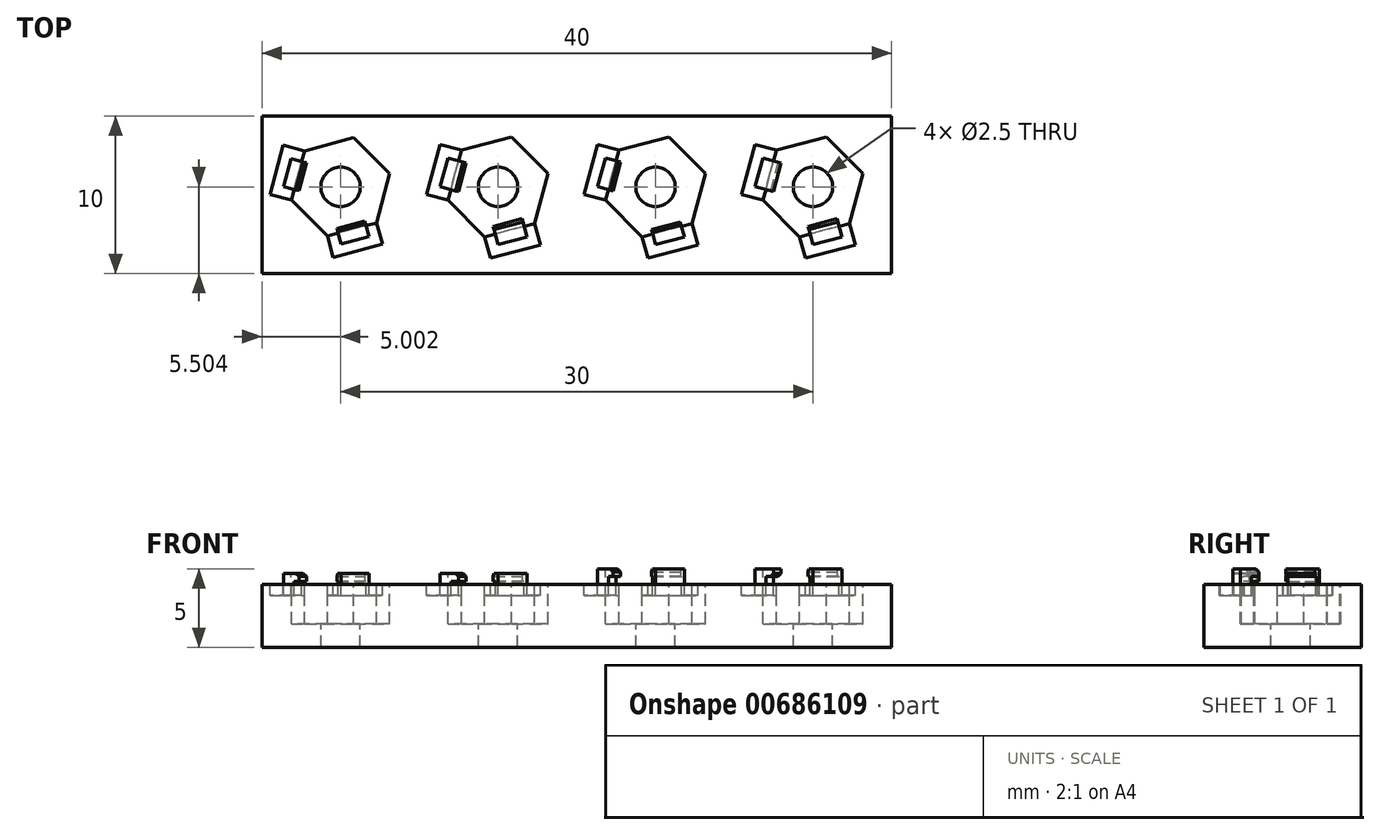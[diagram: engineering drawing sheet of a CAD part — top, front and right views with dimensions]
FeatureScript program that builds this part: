
annotation { "Feature Type Name" : "Feature", "Feature Type Description" : "" }
export const myFeature = defineFeature(function(context is Context, id is Id, definition is map)
    precondition{}
    {
        {
            var Q0;
            Q0=qCreatedBy(makeId("Top.planeOp"),FACE);
            var sketch = newSketch(context, id + "F0", { "sketchPlane" : qUnion([Q0])});
            skLineSegment(sketch, "E0.bottom", {"start": v(-19.43, 38.27) * mm, "end": v(20.57, 38.27) * mm});
            skLineSegment(sketch, "E0.top", {"start": v(-19.43, 28.27) * mm, "end": v(20.57, 28.27) * mm});
            skLineSegment(sketch, "E0.left", {"start": v(-19.43, 38.27) * mm, "end": v(-19.43, 28.27) * mm});
            skLineSegment(sketch, "E0.right", {"start": v(20.57, 38.27) * mm, "end": v(20.57, 28.27) * mm});
            skSolve(sketch);
        }
        {
            var Q0;
            Q0=makeQuery(id+"F0.imprint","IMPRINT",FACE,{"disambiguationData":[TD([[makeQuery(id+"F0.imprint","IMPRINT",EDGE,{"derivedFrom":sQuery(id+"F0.wireOp",EDGE,"E0.bottom")}),-1.0]])]});
            extrude(context, id + "F1", {"entities" : qUnion([Q0]), "depth" : 4 * mm, "offsetDistance" : 25 * mm});
        }
        {
            var Q0;
            Q0=makeQuery(id+"F1.opExtrude","CAP_FACE",FACE,{"disambiguationData":[OSD([sQuery(id+"F0.wireOp",EDGE,"E0.bottom"),sQuery(id+"F0.wireOp",EDGE,"E0.top"),sQuery(id+"F0.wireOp",EDGE,"E0.left"),sQuery(id+"F0.wireOp",EDGE,"E0.right")])],"isStart":false});
            var sketch = newSketch(context, id + "F2", { "sketchPlane" : qUnion([Q0])});
            skCircle(sketch, "E1.cCircle", {"center": v(-14.43, 33.77) * mm, "radius": 2.8 * mm, "construction": true});
            skLineSegment(sketch, "E1.0", {"start": v(-15.27, 30.65) * mm, "end": v(-17.55, 32.94) * mm});
            skLineSegment(sketch, "E1.1", {"start": v(-17.55, 32.94) * mm, "end": v(-16.71, 36.06) * mm});
            skLineSegment(sketch, "E1.2", {"start": v(-16.71, 36.06) * mm, "end": v(-13.6, 36.9) * mm});
            skLineSegment(sketch, "E1.3", {"start": v(-13.6, 36.9) * mm, "end": v(-11.3, 34.61) * mm});
            skLineSegment(sketch, "E1.4", {"start": v(-11.3, 34.61) * mm, "end": v(-12.14, 31.49) * mm});
            skLineSegment(sketch, "E1.5", {"start": v(-12.14, 31.49) * mm, "end": v(-15.27, 30.65) * mm});
            skPoint(sketch, "E1.0.midPoint", {"position": v(-16.4, 31.8) * mm});
            skLineSegment(sketch, "E2", {"start": v(-16.9, 35.38) * mm, "end": v(-17.57, 35.57) * mm});
            skLineSegment(sketch, "E3", {"start": v(-17.57, 35.57) * mm, "end": v(-18.05, 33.8) * mm});
            skLineSegment(sketch, "E4", {"start": v(-18.05, 33.8) * mm, "end": v(-17.37, 33.61) * mm});
            skLineSegment(sketch, "E5", {"start": v(-17.55, 32.94) * mm, "end": v(-18.9, 33.3) * mm});
            skLineSegment(sketch, "E6", {"start": v(-18.9, 33.3) * mm, "end": v(-18.07, 36.42) * mm});
            skLineSegment(sketch, "E7", {"start": v(-18.07, 36.42) * mm, "end": v(-16.71, 36.06) * mm});
            skLineSegment(sketch, "E8", {"start": v(-17.37, 33.61) * mm, "end": v(-17.08, 33.54) * mm});
            skLineSegment(sketch, "E9", {"start": v(-17.08, 33.54) * mm, "end": v(-16.6, 35.3) * mm});
            skLineSegment(sketch, "E10", {"start": v(-16.6, 35.3) * mm, "end": v(-16.9, 35.38) * mm});
            skLineSegment(sketch, "E11", {"start": v(-15.27, 30.65) * mm, "end": v(-14.9, 29.3) * mm});
            skLineSegment(sketch, "E12", {"start": v(-14.9, 29.3) * mm, "end": v(-11.78, 30.14) * mm});
            skLineSegment(sketch, "E13", {"start": v(-11.78, 30.14) * mm, "end": v(-12.14, 31.49) * mm});
            skLineSegment(sketch, "E14", {"start": v(-14.59, 30.83) * mm, "end": v(-14.4, 30.16) * mm});
            skLineSegment(sketch, "E15", {"start": v(-14.4, 30.16) * mm, "end": v(-12.64, 30.63) * mm});
            skLineSegment(sketch, "E16", {"start": v(-12.64, 30.63) * mm, "end": v(-12.82, 31.3) * mm});
            skLineSegment(sketch, "E17", {"start": v(-14.59, 30.83) * mm, "end": v(-14.67, 31.12) * mm});
            skLineSegment(sketch, "E18", {"start": v(-14.67, 31.12) * mm, "end": v(-12.9, 31.6) * mm});
            skLineSegment(sketch, "E19", {"start": v(-12.9, 31.6) * mm, "end": v(-12.82, 31.3) * mm});
            skCircle(sketch, "E20.cCircle", {"center": v(-4.43, 33.77) * mm, "radius": 2.85 * mm, "construction": true});
            skLineSegment(sketch, "E20.0", {"start": v(-5.28, 30.6) * mm, "end": v(-7.6, 32.92) * mm});
            skLineSegment(sketch, "E20.1", {"start": v(-7.6, 32.92) * mm, "end": v(-6.76, 36.1) * mm});
            skLineSegment(sketch, "E20.2", {"start": v(-6.76, 36.1) * mm, "end": v(-3.58, 36.95) * mm});
            skLineSegment(sketch, "E20.3", {"start": v(-3.58, 36.95) * mm, "end": v(-1.25, 34.63) * mm});
            skLineSegment(sketch, "E20.4", {"start": v(-1.25, 34.63) * mm, "end": v(-2.1, 31.45) * mm});
            skLineSegment(sketch, "E20.5", {"start": v(-2.1, 31.45) * mm, "end": v(-5.28, 30.6) * mm});
            skPoint(sketch, "E20.0.midPoint", {"position": v(-6.44, 31.76) * mm});
            skLineSegment(sketch, "E21", {"start": v(-6.94, 35.42) * mm, "end": v(-7.61, 35.6) * mm});
            skLineSegment(sketch, "E22", {"start": v(-7.61, 35.6) * mm, "end": v(-8.1, 33.78) * mm});
            skLineSegment(sketch, "E23", {"start": v(-8.1, 33.78) * mm, "end": v(-7.43, 33.6) * mm});
            skLineSegment(sketch, "E24", {"start": v(-7.6, 32.92) * mm, "end": v(-8.96, 33.28) * mm});
            skLineSegment(sketch, "E25", {"start": v(-8.96, 33.28) * mm, "end": v(-8.1, 36.46) * mm});
            skLineSegment(sketch, "E26", {"start": v(-8.1, 36.46) * mm, "end": v(-6.76, 36.1) * mm});
            skLineSegment(sketch, "E27", {"start": v(-7.43, 33.6) * mm, "end": v(-7.04, 33.5) * mm});
            skLineSegment(sketch, "E28", {"start": v(-7.04, 33.5) * mm, "end": v(-6.55, 35.32) * mm});
            skLineSegment(sketch, "E29", {"start": v(-6.55, 35.32) * mm, "end": v(-6.94, 35.42) * mm});
            skLineSegment(sketch, "E30", {"start": v(-5.28, 30.6) * mm, "end": v(-4.92, 29.24) * mm});
            skLineSegment(sketch, "E31", {"start": v(-4.92, 29.24) * mm, "end": v(-1.74, 30.1) * mm});
            skLineSegment(sketch, "E32", {"start": v(-1.74, 30.1) * mm, "end": v(-2.1, 31.45) * mm});
            skLineSegment(sketch, "E33", {"start": v(-4.6, 30.78) * mm, "end": v(-4.42, 30.1) * mm});
            skLineSegment(sketch, "E34", {"start": v(-4.42, 30.1) * mm, "end": v(-2.6, 30.59) * mm});
            skLineSegment(sketch, "E35", {"start": v(-2.6, 30.59) * mm, "end": v(-2.78, 31.27) * mm});
            skLineSegment(sketch, "E36", {"start": v(-4.6, 30.78) * mm, "end": v(-4.7, 31.16) * mm});
            skLineSegment(sketch, "E37", {"start": v(-4.7, 31.16) * mm, "end": v(-2.88, 31.65) * mm});
            skLineSegment(sketch, "E38", {"start": v(-2.88, 31.65) * mm, "end": v(-2.78, 31.27) * mm});
            skCircle(sketch, "E39.cCircle", {"center": v(5.57, 33.77) * mm, "radius": 2.85 * mm, "construction": true});
            skLineSegment(sketch, "E39.0", {"start": v(4.72, 30.6) * mm, "end": v(2.4, 32.92) * mm});
            skLineSegment(sketch, "E39.1", {"start": v(2.4, 32.92) * mm, "end": v(3.24, 36.1) * mm});
            skLineSegment(sketch, "E39.2", {"start": v(3.24, 36.1) * mm, "end": v(6.42, 36.95) * mm});
            skLineSegment(sketch, "E39.3", {"start": v(6.42, 36.95) * mm, "end": v(8.75, 34.63) * mm});
            skLineSegment(sketch, "E39.4", {"start": v(8.75, 34.63) * mm, "end": v(7.9, 31.45) * mm});
            skLineSegment(sketch, "E39.5", {"start": v(7.9, 31.45) * mm, "end": v(4.72, 30.6) * mm});
            skPoint(sketch, "E39.0.midPoint", {"position": v(3.56, 31.76) * mm});
            skLineSegment(sketch, "E40", {"start": v(3.06, 35.42) * mm, "end": v(2.39, 35.6) * mm});
            skLineSegment(sketch, "E41", {"start": v(2.39, 35.6) * mm, "end": v(1.9, 33.78) * mm});
            skLineSegment(sketch, "E42", {"start": v(1.9, 33.78) * mm, "end": v(2.57, 33.6) * mm});
            skLineSegment(sketch, "E43", {"start": v(2.4, 32.92) * mm, "end": v(1.04, 33.28) * mm});
            skLineSegment(sketch, "E44", {"start": v(1.04, 33.28) * mm, "end": v(1.9, 36.46) * mm});
            skLineSegment(sketch, "E45", {"start": v(1.9, 36.46) * mm, "end": v(3.24, 36.1) * mm});
            skLineSegment(sketch, "E46", {"start": v(2.57, 33.6) * mm, "end": v(2.96, 33.5) * mm});
            skLineSegment(sketch, "E47", {"start": v(2.96, 33.5) * mm, "end": v(3.45, 35.32) * mm});
            skLineSegment(sketch, "E48", {"start": v(3.45, 35.32) * mm, "end": v(3.06, 35.42) * mm});
            skLineSegment(sketch, "E49", {"start": v(4.72, 30.6) * mm, "end": v(5.08, 29.24) * mm});
            skLineSegment(sketch, "E50", {"start": v(5.08, 29.24) * mm, "end": v(8.26, 30.1) * mm});
            skLineSegment(sketch, "E51", {"start": v(8.26, 30.1) * mm, "end": v(7.9, 31.45) * mm});
            skLineSegment(sketch, "E52", {"start": v(5.4, 30.78) * mm, "end": v(5.58, 30.1) * mm});
            skLineSegment(sketch, "E53", {"start": v(5.58, 30.1) * mm, "end": v(7.4, 30.59) * mm});
            skLineSegment(sketch, "E54", {"start": v(7.4, 30.59) * mm, "end": v(7.22, 31.27) * mm});
            skLineSegment(sketch, "E55", {"start": v(5.4, 30.78) * mm, "end": v(5.3, 31.16) * mm});
            skLineSegment(sketch, "E56", {"start": v(5.3, 31.16) * mm, "end": v(7.12, 31.65) * mm});
            skLineSegment(sketch, "E57", {"start": v(7.12, 31.65) * mm, "end": v(7.22, 31.27) * mm});
            skCircle(sketch, "E58.cCircle", {"center": v(15.57, 33.77) * mm, "radius": 2.85 * mm, "construction": true});
            skLineSegment(sketch, "E58.0", {"start": v(14.72, 30.6) * mm, "end": v(12.4, 32.92) * mm});
            skLineSegment(sketch, "E58.1", {"start": v(12.4, 32.92) * mm, "end": v(13.24, 36.1) * mm});
            skLineSegment(sketch, "E58.2", {"start": v(13.24, 36.1) * mm, "end": v(16.42, 36.95) * mm});
            skLineSegment(sketch, "E58.3", {"start": v(16.42, 36.95) * mm, "end": v(18.75, 34.63) * mm});
            skLineSegment(sketch, "E58.4", {"start": v(18.75, 34.63) * mm, "end": v(17.9, 31.45) * mm});
            skLineSegment(sketch, "E58.5", {"start": v(17.9, 31.45) * mm, "end": v(14.72, 30.6) * mm});
            skPoint(sketch, "E58.0.midPoint", {"position": v(13.56, 31.76) * mm});
            skLineSegment(sketch, "E59", {"start": v(13.06, 35.42) * mm, "end": v(12.39, 35.6) * mm});
            skLineSegment(sketch, "E60", {"start": v(12.39, 35.6) * mm, "end": v(11.9, 33.78) * mm});
            skLineSegment(sketch, "E61", {"start": v(11.9, 33.78) * mm, "end": v(12.57, 33.6) * mm});
            skLineSegment(sketch, "E62", {"start": v(12.4, 32.92) * mm, "end": v(11.04, 33.28) * mm});
            skLineSegment(sketch, "E63", {"start": v(11.04, 33.28) * mm, "end": v(11.9, 36.46) * mm});
            skLineSegment(sketch, "E64", {"start": v(11.9, 36.46) * mm, "end": v(13.24, 36.1) * mm});
            skLineSegment(sketch, "E65", {"start": v(12.57, 33.6) * mm, "end": v(13.06, 33.47) * mm});
            skLineSegment(sketch, "E66", {"start": v(13.06, 33.47) * mm, "end": v(13.55, 35.3) * mm});
            skLineSegment(sketch, "E67", {"start": v(13.55, 35.3) * mm, "end": v(13.06, 35.42) * mm});
            skLineSegment(sketch, "E68", {"start": v(14.72, 30.6) * mm, "end": v(15.08, 29.24) * mm});
            skLineSegment(sketch, "E69", {"start": v(15.08, 29.24) * mm, "end": v(18.26, 30.1) * mm});
            skLineSegment(sketch, "E70", {"start": v(18.26, 30.1) * mm, "end": v(17.9, 31.45) * mm});
            skLineSegment(sketch, "E71", {"start": v(15.4, 30.78) * mm, "end": v(15.58, 30.1) * mm});
            skLineSegment(sketch, "E72", {"start": v(15.58, 30.1) * mm, "end": v(17.4, 30.59) * mm});
            skLineSegment(sketch, "E73", {"start": v(17.4, 30.59) * mm, "end": v(17.22, 31.27) * mm});
            skLineSegment(sketch, "E74", {"start": v(15.4, 30.78) * mm, "end": v(15.27, 31.26) * mm});
            skLineSegment(sketch, "E75", {"start": v(15.27, 31.26) * mm, "end": v(17.1, 31.75) * mm});
            skLineSegment(sketch, "E76", {"start": v(17.1, 31.75) * mm, "end": v(17.22, 31.27) * mm});
            skLineSegment(sketch, "E77", {"start": v(-14.43, 33.77) * mm, "end": v(-14.43, 38.27) * mm, "construction": true});
            skLineSegment(sketch, "E78", {"start": v(-4.43, 33.77) * mm, "end": v(-4.43, 38.27) * mm, "construction": true});
            skLineSegment(sketch, "E79", {"start": v(5.57, 33.77) * mm, "end": v(5.57, 38.27) * mm, "construction": true});
            skLineSegment(sketch, "E80", {"start": v(15.57, 33.77) * mm, "end": v(15.57, 38.27) * mm, "construction": true});
            skCircle(sketch, "E81", {"center": v(-14.43, 33.77) * mm, "radius": 1.25 * mm});
            skCircle(sketch, "E82", {"center": v(-4.43, 33.77) * mm, "radius": 1.25 * mm});
            skCircle(sketch, "E83", {"center": v(5.57, 33.77) * mm, "radius": 1.25 * mm});
            skCircle(sketch, "E84", {"center": v(15.57, 33.77) * mm, "radius": 1.25 * mm});
            skSolve(sketch);
        }
        {
            var Q0;
            {var subQ1=sQuery(id+"F2.wireOp",EDGE,"E1.0");Q0=makeQuery(id+"F2.imprint","IMPRINT",FACE,{"disambiguationData":[TD([[makeQuery(id+"F2.imprint","IMPRINT",EDGE,{"derivedFrom":subQ1}),-1.0]])]});}
            var Q1;
            {var subQ0=sQuery(id+"F2.wireOp",EDGE,"E17");Q1=makeQuery(id+"F2.imprint","IMPRINT",FACE,{"disambiguationData":[TD([[makeQuery(id+"F2.imprint","IMPRINT",EDGE,{"derivedFrom":subQ0}),-1.0]])]});}
            var Q2;
            {var subQ2=sQuery(id+"F2.wireOp",EDGE,"E8");Q2=makeQuery(id+"F2.imprint","IMPRINT",FACE,{"disambiguationData":[TD([[makeQuery(id+"F2.imprint","IMPRINT",EDGE,{"derivedFrom":subQ2}),1.0]])]});}
            var Q3;
            {var subQ1=sQuery(id+"F2.wireOp",EDGE,"E20.0");Q3=makeQuery(id+"F2.imprint","IMPRINT",FACE,{"disambiguationData":[TD([[makeQuery(id+"F2.imprint","IMPRINT",EDGE,{"derivedFrom":subQ1}),-1.0]])]});}
            var Q4;
            {var subQ0=sQuery(id+"F2.wireOp",EDGE,"E36");Q4=makeQuery(id+"F2.imprint","IMPRINT",FACE,{"disambiguationData":[TD([[makeQuery(id+"F2.imprint","IMPRINT",EDGE,{"derivedFrom":subQ0}),-1.0]])]});}
            var Q5;
            {var subQ2=sQuery(id+"F2.wireOp",EDGE,"E27");Q5=makeQuery(id+"F2.imprint","IMPRINT",FACE,{"disambiguationData":[TD([[makeQuery(id+"F2.imprint","IMPRINT",EDGE,{"derivedFrom":subQ2}),1.0]])]});}
            var Q6;
            {var subQ1=sQuery(id+"F2.wireOp",EDGE,"E39.0");Q6=makeQuery(id+"F2.imprint","IMPRINT",FACE,{"disambiguationData":[TD([[makeQuery(id+"F2.imprint","IMPRINT",EDGE,{"derivedFrom":subQ1}),-1.0]])]});}
            var Q7;
            {var subQ2=sQuery(id+"F2.wireOp",EDGE,"E46");Q7=makeQuery(id+"F2.imprint","IMPRINT",FACE,{"disambiguationData":[TD([[makeQuery(id+"F2.imprint","IMPRINT",EDGE,{"derivedFrom":subQ2}),1.0]])]});}
            var Q8;
            {var subQ0=sQuery(id+"F2.wireOp",EDGE,"E55");Q8=makeQuery(id+"F2.imprint","IMPRINT",FACE,{"disambiguationData":[TD([[makeQuery(id+"F2.imprint","IMPRINT",EDGE,{"derivedFrom":subQ0}),-1.0]])]});}
            var Q9;
            {var subQ1=sQuery(id+"F2.wireOp",EDGE,"E58.0");Q9=makeQuery(id+"F2.imprint","IMPRINT",FACE,{"disambiguationData":[TD([[makeQuery(id+"F2.imprint","IMPRINT",EDGE,{"derivedFrom":subQ1}),-1.0]])]});}
            var Q10;
            {var subQ0=sQuery(id+"F2.wireOp",EDGE,"E74");Q10=makeQuery(id+"F2.imprint","IMPRINT",FACE,{"disambiguationData":[TD([[makeQuery(id+"F2.imprint","IMPRINT",EDGE,{"derivedFrom":subQ0}),-1.0]])]});}
            var Q11;
            {var subQ2=sQuery(id+"F2.wireOp",EDGE,"E65");Q11=makeQuery(id+"F2.imprint","IMPRINT",FACE,{"disambiguationData":[TD([[makeQuery(id+"F2.imprint","IMPRINT",EDGE,{"derivedFrom":subQ2}),1.0]])]});}
            extrude(context, id + "F3", {"entities" : qUnion([Q0, Q1, Q2, Q3, Q4, Q5, Q6, Q7, Q8, Q9, Q10, Q11]), "operationType" : NewBodyOperationType.REMOVE, "oppositeDirection" : true, "depth" : 2.5 * mm, "offsetDistance" : 25 * mm});
        }
        {
            var Q0;
            {var subQ0=sQuery(id+"F2.wireOp",EDGE,"E2");Q0=makeQuery(id+"F2.imprint","IMPRINT",FACE,{"disambiguationData":[TD([[makeQuery(id+"F2.imprint","IMPRINT",EDGE,{"derivedFrom":subQ0}),-1.0]])]});}
            var Q1;
            {var subQ0=sQuery(id+"F2.wireOp",EDGE,"E11");Q1=makeQuery(id+"F2.imprint","IMPRINT",FACE,{"disambiguationData":[TD([[makeQuery(id+"F2.imprint","IMPRINT",EDGE,{"derivedFrom":subQ0}),1.0]])]});}
            var Q2;
            {var subQ0=sQuery(id+"F2.wireOp",EDGE,"E30");Q2=makeQuery(id+"F2.imprint","IMPRINT",FACE,{"disambiguationData":[TD([[makeQuery(id+"F2.imprint","IMPRINT",EDGE,{"derivedFrom":subQ0}),1.0]])]});}
            var Q3;
            {var subQ0=sQuery(id+"F2.wireOp",EDGE,"E21");Q3=makeQuery(id+"F2.imprint","IMPRINT",FACE,{"disambiguationData":[TD([[makeQuery(id+"F2.imprint","IMPRINT",EDGE,{"derivedFrom":subQ0}),-1.0]])]});}
            var Q4;
            {var subQ0=sQuery(id+"F2.wireOp",EDGE,"E40");Q4=makeQuery(id+"F2.imprint","IMPRINT",FACE,{"disambiguationData":[TD([[makeQuery(id+"F2.imprint","IMPRINT",EDGE,{"derivedFrom":subQ0}),-1.0]])]});}
            var Q5;
            {var subQ0=sQuery(id+"F2.wireOp",EDGE,"E49");Q5=makeQuery(id+"F2.imprint","IMPRINT",FACE,{"disambiguationData":[TD([[makeQuery(id+"F2.imprint","IMPRINT",EDGE,{"derivedFrom":subQ0}),1.0]])]});}
            var Q6;
            {var subQ0=sQuery(id+"F2.wireOp",EDGE,"E68");Q6=makeQuery(id+"F2.imprint","IMPRINT",FACE,{"disambiguationData":[TD([[makeQuery(id+"F2.imprint","IMPRINT",EDGE,{"derivedFrom":subQ0}),1.0]])]});}
            var Q7;
            {var subQ0=sQuery(id+"F2.wireOp",EDGE,"E59");Q7=makeQuery(id+"F2.imprint","IMPRINT",FACE,{"disambiguationData":[TD([[makeQuery(id+"F2.imprint","IMPRINT",EDGE,{"derivedFrom":subQ0}),-1.0]])]});}
            extrude(context, id + "F4", {"entities" : qUnion([Q0, Q1, Q2, Q3, Q4, Q5, Q6, Q7]), "operationType" : NewBodyOperationType.REMOVE, "oppositeDirection" : true, "depth" : .7 * mm, "offsetDistance" : 25 * mm});
        }
        {
            var Q0;
            {var subQ0=sQuery(id+"F2.wireOp",EDGE,"E2");Q0=makeQuery(id+"F2.imprint","IMPRINT",FACE,{"disambiguationData":[TD([[makeQuery(id+"F2.imprint","IMPRINT",EDGE,{"derivedFrom":subQ0}),1.0]])]});}
            var Q1;
            {var subQ0=sQuery(id+"F2.wireOp",EDGE,"E14");Q1=makeQuery(id+"F2.imprint","IMPRINT",FACE,{"disambiguationData":[TD([[makeQuery(id+"F2.imprint","IMPRINT",EDGE,{"derivedFrom":subQ0}),1.0]])]});}
            var Q2;
            {var subQ0=sQuery(id+"F2.wireOp",EDGE,"E33");Q2=makeQuery(id+"F2.imprint","IMPRINT",FACE,{"disambiguationData":[TD([[makeQuery(id+"F2.imprint","IMPRINT",EDGE,{"derivedFrom":subQ0}),1.0]])]});}
            var Q3;
            {var subQ0=sQuery(id+"F2.wireOp",EDGE,"E21");Q3=makeQuery(id+"F2.imprint","IMPRINT",FACE,{"disambiguationData":[TD([[makeQuery(id+"F2.imprint","IMPRINT",EDGE,{"derivedFrom":subQ0}),1.0]])]});}
            extrude(context, id + "F5", {"entities" : qUnion([Q0, Q1, Q2, Q3]), "operationType" : NewBodyOperationType.ADD, "depth" : .2 * mm, "offsetDistance" : 25 * mm});
        }
        {
            var Q0;
            {var subQ0=sQuery(id+"F2.wireOp",EDGE,"E40");Q0=makeQuery(id+"F2.imprint","IMPRINT",FACE,{"disambiguationData":[TD([[makeQuery(id+"F2.imprint","IMPRINT",EDGE,{"derivedFrom":subQ0}),1.0]])]});}
            var Q1;
            {var subQ0=sQuery(id+"F2.wireOp",EDGE,"E52");Q1=makeQuery(id+"F2.imprint","IMPRINT",FACE,{"disambiguationData":[TD([[makeQuery(id+"F2.imprint","IMPRINT",EDGE,{"derivedFrom":subQ0}),1.0]])]});}
            var Q2;
            {var subQ0=sQuery(id+"F2.wireOp",EDGE,"E59");Q2=makeQuery(id+"F2.imprint","IMPRINT",FACE,{"disambiguationData":[TD([[makeQuery(id+"F2.imprint","IMPRINT",EDGE,{"derivedFrom":subQ0}),1.0]])]});}
            var Q3;
            {var subQ0=sQuery(id+"F2.wireOp",EDGE,"E71");Q3=makeQuery(id+"F2.imprint","IMPRINT",FACE,{"disambiguationData":[TD([[makeQuery(id+"F2.imprint","IMPRINT",EDGE,{"derivedFrom":subQ0}),1.0]])]});}
            extrude(context, id + "F6", {"entities" : qUnion([Q0, Q1, Q2, Q3]), "operationType" : NewBodyOperationType.ADD, "depth" : .5 * mm, "offsetDistance" : 25 * mm});
        }
        {
            var Q0;
            Q0=makeQuery(id+"F3.boolean.opBoolean","SPLIT",FACE,{"disambiguationData":[TD([makeQuery(id+"F3.opExtrude","SWEPT_FACE",FACE,{"disambiguationData":[OSD([sQuery(id+"F2.wireOp",EDGE,"E81")])]})])],"derivedFrom":makeQuery(id+"F1.opExtrude","CAP_FACE",FACE,{"disambiguationData":[OSD([sQuery(id+"F0.wireOp",EDGE,"E0.bottom"),sQuery(id+"F0.wireOp",EDGE,"E0.top"),sQuery(id+"F0.wireOp",EDGE,"E0.left"),sQuery(id+"F0.wireOp",EDGE,"E0.right")])],"isStart":false})});
            var Q1;
            Q1=makeQuery(id+"F3.boolean.opBoolean","SPLIT",FACE,{"disambiguationData":[TD([makeQuery(id+"F3.opExtrude","SWEPT_FACE",FACE,{"disambiguationData":[OSD([sQuery(id+"F2.wireOp",EDGE,"E82")])]})])],"derivedFrom":makeQuery(id+"F1.opExtrude","CAP_FACE",FACE,{"disambiguationData":[OSD([sQuery(id+"F0.wireOp",EDGE,"E0.bottom"),sQuery(id+"F0.wireOp",EDGE,"E0.top"),sQuery(id+"F0.wireOp",EDGE,"E0.left"),sQuery(id+"F0.wireOp",EDGE,"E0.right")])],"isStart":false})});
            var Q2;
            Q2=makeQuery(id+"F3.boolean.opBoolean","SPLIT",FACE,{"disambiguationData":[TD([makeQuery(id+"F3.opExtrude","SWEPT_FACE",FACE,{"disambiguationData":[OSD([sQuery(id+"F2.wireOp",EDGE,"E83")])]})])],"derivedFrom":makeQuery(id+"F1.opExtrude","CAP_FACE",FACE,{"disambiguationData":[OSD([sQuery(id+"F0.wireOp",EDGE,"E0.bottom"),sQuery(id+"F0.wireOp",EDGE,"E0.top"),sQuery(id+"F0.wireOp",EDGE,"E0.left"),sQuery(id+"F0.wireOp",EDGE,"E0.right")])],"isStart":false})});
            var Q3;
            Q3=makeQuery(id+"F3.boolean.opBoolean","SPLIT",FACE,{"disambiguationData":[TD([makeQuery(id+"F3.opExtrude","SWEPT_FACE",FACE,{"disambiguationData":[OSD([sQuery(id+"F2.wireOp",EDGE,"E84")])]})])],"derivedFrom":makeQuery(id+"F1.opExtrude","CAP_FACE",FACE,{"disambiguationData":[OSD([sQuery(id+"F0.wireOp",EDGE,"E0.bottom"),sQuery(id+"F0.wireOp",EDGE,"E0.top"),sQuery(id+"F0.wireOp",EDGE,"E0.left"),sQuery(id+"F0.wireOp",EDGE,"E0.right")])],"isStart":false})});
            extrude(context, id + "F7", {"entities" : qUnion([Q0, Q1, Q2, Q3]), "operationType" : NewBodyOperationType.REMOVE, "oppositeDirection" : true, "depth" : 25 * mm, "offsetDistance" : 25 * mm});
        }
        {
            var Q0;
            Q0=makeQuery(id+"F5.opExtrude","CAP_FACE",FACE,{"disambiguationData":[OSD([sQuery(id+"F2.wireOp",EDGE,"E1.1"),sQuery(id+"F2.wireOp",EDGE,"E2"),sQuery(id+"F2.wireOp",EDGE,"E3"),sQuery(id+"F2.wireOp",EDGE,"E4")])],"isStart":false});
            var sketch = newSketch(context, id + "F8", { "sketchPlane" : qUnion([Q0])});
            skLineSegment(sketch, "E85.0.0", {"start": v(-18.05, 33.8) * mm, "end": v(-17.37, 33.61) * mm});
            skLineSegment(sketch, "E85.0.1", {"start": v(-17.37, 33.61) * mm, "end": v(-16.9, 35.38) * mm});
            skLineSegment(sketch, "E85.0.2", {"start": v(-16.9, 35.38) * mm, "end": v(-17.57, 35.57) * mm});
            skLineSegment(sketch, "E85.0.3", {"start": v(-17.57, 35.57) * mm, "end": v(-18.05, 33.8) * mm});
            skLineSegment(sketch, "E86.0.0", {"start": v(-14.4, 30.16) * mm, "end": v(-12.64, 30.63) * mm});
            skLineSegment(sketch, "E86.0.1", {"start": v(-12.64, 30.63) * mm, "end": v(-12.82, 31.3) * mm});
            skLineSegment(sketch, "E86.0.3", {"start": v(-14.59, 30.83) * mm, "end": v(-14.4, 30.16) * mm});
            skLineSegment(sketch, "E87.0.0", {"start": v(-8.1, 33.78) * mm, "end": v(-7.43, 33.6) * mm});
            skLineSegment(sketch, "E87.0.1", {"start": v(-7.43, 33.6) * mm, "end": v(-6.94, 35.42) * mm});
            skLineSegment(sketch, "E87.0.2", {"start": v(-6.94, 35.42) * mm, "end": v(-7.61, 35.6) * mm});
            skLineSegment(sketch, "E87.0.3", {"start": v(-7.61, 35.6) * mm, "end": v(-8.1, 33.78) * mm});
            skLineSegment(sketch, "E88.0.0", {"start": v(-4.42, 30.1) * mm, "end": v(-2.6, 30.59) * mm});
            skLineSegment(sketch, "E88.0.1", {"start": v(-2.6, 30.59) * mm, "end": v(-2.78, 31.27) * mm});
            skLineSegment(sketch, "E88.0.2", {"start": v(-2.78, 31.27) * mm, "end": v(-4.6, 30.78) * mm});
            skLineSegment(sketch, "E88.0.3", {"start": v(-4.6, 30.78) * mm, "end": v(-4.42, 30.1) * mm});
            skLineSegment(sketch, "E89", {"start": v(-17.37, 33.61) * mm, "end": v(-17.08, 33.54) * mm});
            skLineSegment(sketch, "E90", {"start": v(-17.08, 33.54) * mm, "end": v(-16.6, 35.3) * mm});
            skLineSegment(sketch, "E91", {"start": v(-16.6, 35.3) * mm, "end": v(-16.9, 35.38) * mm});
            skLineSegment(sketch, "E92", {"start": v(-7.43, 33.6) * mm, "end": v(-6.94, 33.47) * mm});
            skLineSegment(sketch, "E93", {"start": v(-6.94, 33.47) * mm, "end": v(-6.45, 35.3) * mm});
            skLineSegment(sketch, "E94", {"start": v(-6.45, 35.3) * mm, "end": v(-6.94, 35.42) * mm});
            skLineSegment(sketch, "E95", {"start": v(-4.6, 30.78) * mm, "end": v(-4.73, 31.26) * mm});
            skLineSegment(sketch, "E96", {"start": v(-4.73, 31.26) * mm, "end": v(-2.9, 31.75) * mm});
            skLineSegment(sketch, "E97", {"start": v(-2.9, 31.75) * mm, "end": v(-2.78, 31.27) * mm});
            skLineSegment(sketch, "E98", {"start": v(-14.59, 30.83) * mm, "end": v(-14.67, 31.12) * mm});
            skLineSegment(sketch, "E99", {"start": v(-14.67, 31.12) * mm, "end": v(-12.9, 31.6) * mm});
            skLineSegment(sketch, "E100", {"start": v(-12.9, 31.6) * mm, "end": v(-12.82, 31.3) * mm});
            skSolve(sketch);
        }
        {
            var Q0;
            Q0=qSketchRegion(id+"F8",true);
            extrude(context, id + "F9", {"entities" : qUnion([Q0]), "operationType" : NewBodyOperationType.ADD, "depth" : .5 * mm, "offsetDistance" : 25 * mm});
        }
        {
            var Q0;
            Q0=makeQuery(id+"F6.opExtrude","CAP_FACE",FACE,{"disambiguationData":[OSD([sQuery(id+"F2.wireOp",EDGE,"E39.1"),sQuery(id+"F2.wireOp",EDGE,"E40"),sQuery(id+"F2.wireOp",EDGE,"E41"),sQuery(id+"F2.wireOp",EDGE,"E42")])],"isStart":false});
            var sketch = newSketch(context, id + "F10", { "sketchPlane" : qUnion([Q0])});
            skLineSegment(sketch, "E101.0.0", {"start": v(1.9, 33.78) * mm, "end": v(2.57, 33.6) * mm});
            skLineSegment(sketch, "E101.0.1", {"start": v(2.57, 33.6) * mm, "end": v(3.06, 35.42) * mm});
            skLineSegment(sketch, "E101.0.2", {"start": v(3.06, 35.42) * mm, "end": v(2.39, 35.6) * mm});
            skLineSegment(sketch, "E101.0.3", {"start": v(2.39, 35.6) * mm, "end": v(1.9, 33.78) * mm});
            skLineSegment(sketch, "E102.0.0", {"start": v(5.58, 30.1) * mm, "end": v(7.4, 30.59) * mm});
            skLineSegment(sketch, "E102.0.1", {"start": v(7.4, 30.59) * mm, "end": v(7.22, 31.27) * mm});
            skLineSegment(sketch, "E102.0.2", {"start": v(7.22, 31.27) * mm, "end": v(5.4, 30.78) * mm});
            skLineSegment(sketch, "E102.0.3", {"start": v(5.4, 30.78) * mm, "end": v(5.58, 30.1) * mm});
            skLineSegment(sketch, "E103.0.0", {"start": v(11.9, 33.78) * mm, "end": v(12.57, 33.6) * mm});
            skLineSegment(sketch, "E103.0.1", {"start": v(12.57, 33.6) * mm, "end": v(13.06, 35.42) * mm});
            skLineSegment(sketch, "E103.0.2", {"start": v(13.06, 35.42) * mm, "end": v(12.39, 35.6) * mm});
            skLineSegment(sketch, "E103.0.3", {"start": v(12.39, 35.6) * mm, "end": v(11.9, 33.78) * mm});
            skLineSegment(sketch, "E104.0.0", {"start": v(15.58, 30.1) * mm, "end": v(17.4, 30.59) * mm});
            skLineSegment(sketch, "E104.0.1", {"start": v(17.4, 30.59) * mm, "end": v(17.22, 31.27) * mm});
            skLineSegment(sketch, "E104.0.2", {"start": v(17.22, 31.27) * mm, "end": v(15.4, 30.78) * mm});
            skLineSegment(sketch, "E104.0.3", {"start": v(15.4, 30.78) * mm, "end": v(15.58, 30.1) * mm});
            skLineSegment(sketch, "E105", {"start": v(3.06, 35.42) * mm, "end": v(3.35, 35.35) * mm});
            skLineSegment(sketch, "E106", {"start": v(3.35, 35.35) * mm, "end": v(2.86, 33.52) * mm});
            skLineSegment(sketch, "E107", {"start": v(2.86, 33.52) * mm, "end": v(2.57, 33.6) * mm});
            skLineSegment(sketch, "E108", {"start": v(5.4, 30.78) * mm, "end": v(5.32, 31.07) * mm});
            skLineSegment(sketch, "E109", {"start": v(5.32, 31.07) * mm, "end": v(7.14, 31.56) * mm});
            skLineSegment(sketch, "E110", {"start": v(7.14, 31.56) * mm, "end": v(7.22, 31.27) * mm});
            skLineSegment(sketch, "E111", {"start": v(12.57, 33.6) * mm, "end": v(13.06, 33.47) * mm});
            skLineSegment(sketch, "E112", {"start": v(13.06, 33.47) * mm, "end": v(13.55, 35.3) * mm});
            skLineSegment(sketch, "E113", {"start": v(13.55, 35.3) * mm, "end": v(13.06, 35.42) * mm});
            skLineSegment(sketch, "E114", {"start": v(15.4, 30.78) * mm, "end": v(15.27, 31.26) * mm});
            skLineSegment(sketch, "E115", {"start": v(15.27, 31.26) * mm, "end": v(17.1, 31.75) * mm});
            skLineSegment(sketch, "E116", {"start": v(17.1, 31.75) * mm, "end": v(17.22, 31.27) * mm});
            skSolve(sketch);
        }
        {
            var Q0;
            Q0=qSketchRegion(id+"F10",true);
            extrude(context, id + "F11", {"entities" : qUnion([Q0]), "operationType" : NewBodyOperationType.ADD, "depth" : .5 * mm, "offsetDistance" : 25 * mm});
        }
        {
            var Q0;
            Q0=makeQuery(id+"F9.opExtrude","CAP_EDGE",EDGE,{"disambiguationData":[OSD([sQuery(id+"F8.wireOp",EDGE,"E90")])],"isStart":false});
            var Q1;
            Q1=makeQuery(id+"F9.opExtrude","CAP_EDGE",EDGE,{"disambiguationData":[OSD([sQuery(id+"F8.wireOp",EDGE,"E99")])],"isStart":false});
            var Q2;
            Q2=makeQuery(id+"F9.opExtrude","CAP_EDGE",EDGE,{"disambiguationData":[OSD([sQuery(id+"F8.wireOp",EDGE,"E93")])],"isStart":false});
            var Q3;
            Q3=makeQuery(id+"F9.opExtrude","CAP_EDGE",EDGE,{"disambiguationData":[OSD([sQuery(id+"F8.wireOp",EDGE,"E96")])],"isStart":false});
            var Q4;
            Q4=makeQuery(id+"F11.opExtrude","CAP_EDGE",EDGE,{"disambiguationData":[OSD([sQuery(id+"F10.wireOp",EDGE,"E106")])],"isStart":false});
            var Q5;
            Q5=makeQuery(id+"F11.opExtrude","CAP_EDGE",EDGE,{"disambiguationData":[OSD([sQuery(id+"F10.wireOp",EDGE,"E109")])],"isStart":false});
            var Q6;
            Q6=makeQuery(id+"F11.opExtrude","CAP_EDGE",EDGE,{"disambiguationData":[OSD([sQuery(id+"F10.wireOp",EDGE,"E112")])],"isStart":true});
            var Q7;
            Q7=makeQuery(id+"F11.opExtrude","CAP_EDGE",EDGE,{"disambiguationData":[OSD([sQuery(id+"F10.wireOp",EDGE,"E115")])],"isStart":false});
            chamfer(context, id + "F12", {"entities" : qUnion([Q0, Q1, Q2, Q3, Q4, Q5, Q6, Q7]), "width" : .2 * mm, "tangentPropagation" : true});
        }
    });
